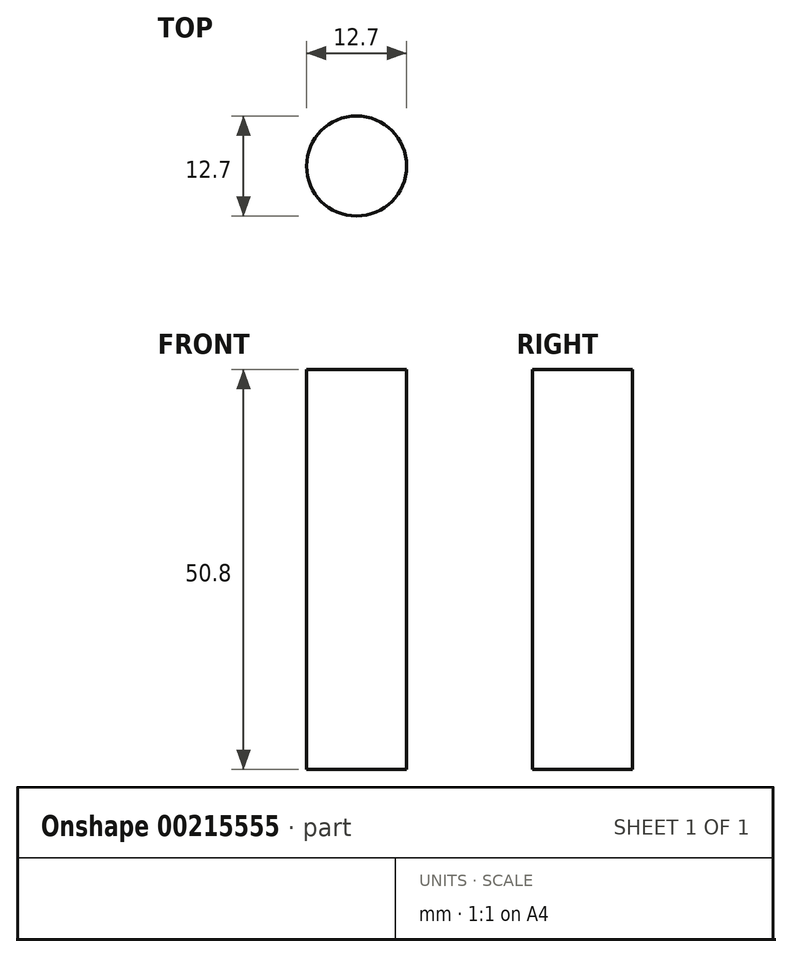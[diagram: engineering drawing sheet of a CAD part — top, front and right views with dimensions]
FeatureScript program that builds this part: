
annotation { "Feature Type Name" : "Feature", "Feature Type Description" : "" }
export const myFeature = defineFeature(function(context is Context, id is Id, definition is map)
    precondition{}
    {
        {
            var Q0;
            Q0=qCreatedBy(makeId("Front.planeOp"),FACE);
            var sketch = newSketch(context, id + "F0", { "sketchPlane" : qUnion([Q0])});
            skLineSegment(sketch, "E0", {"start": v(-14.09, 0) * mm, "end": v(-14.09, 50.8) * mm});
            skSolve(sketch);
        }
        {
            var Q0;
            Q0=qCreatedBy(makeId("Top.planeOp"),FACE);
            var sketch = newSketch(context, id + "F1", { "sketchPlane" : qUnion([Q0])});
            skCircle(sketch, "E1", {"center": v(-14.09, 0) * mm, "radius": 6.35 * mm});
            skSolve(sketch);
        }
        {
            var Q0;
            Q0=makeQuery(id+"F1.imprint","IMPRINT",FACE,{"disambiguationData":[TD([[makeQuery(id+"F1.imprint","IMPRINT",EDGE,{"derivedFrom":sQuery(id+"F1.wireOp",EDGE,"E1")}),1.0]])]});
            var Q1;
            Q1 = qConstructionFilter(qBodyType(qCreatedBy(id + "F0" ,EDGE), BodyType.WIRE), ConstructionObject.NO);
            sweep(context, id + "F2", {"profiles" : qUnion([Q0]), "path" : qUnion([Q1])});
        }
    });
